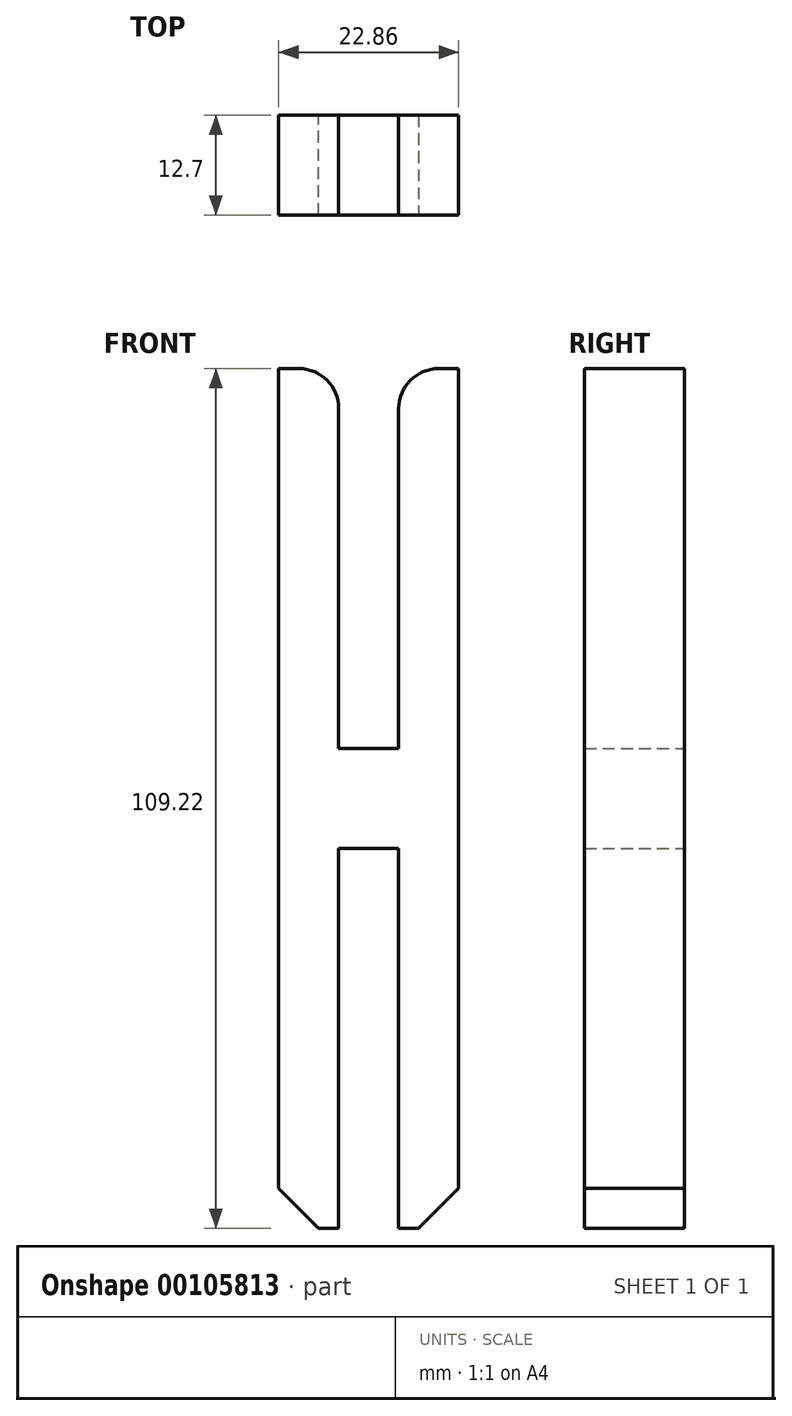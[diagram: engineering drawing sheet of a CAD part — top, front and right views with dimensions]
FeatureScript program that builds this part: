
annotation { "Feature Type Name" : "Feature", "Feature Type Description" : "" }
export const myFeature = defineFeature(function(context is Context, id is Id, definition is map)
    precondition{}
    {
        {
            var Q0;
            Q0=qCreatedBy(makeId("Front.planeOp"),FACE);
            var sketch = newSketch(context, id + "F0", { "sketchPlane" : qUnion([Q0])});
            skLineSegment(sketch, "E0.bottom", {"start": v(11.43, 54.61) * mm, "end": v(-11.43, 54.61) * mm});
            skLineSegment(sketch, "E0.top", {"start": v(11.43, -54.61) * mm, "end": v(-11.43, -54.61) * mm});
            skLineSegment(sketch, "E0.left", {"start": v(11.43, 54.61) * mm, "end": v(11.43, -54.61) * mm});
            skLineSegment(sketch, "E0.right", {"start": v(-11.43, 54.61) * mm, "end": v(-11.43, -54.61) * mm});
            skPoint(sketch, "E0.middle", {"position": v(0, 0) * mm});
            skLineSegment(sketch, "E1.bottom", {"start": v(-3.8, 6.35) * mm, "end": v(3.81, 6.35) * mm});
            skLineSegment(sketch, "E1.top", {"start": v(-3.8, 54.6) * mm, "end": v(3.81, 54.6) * mm});
            skLineSegment(sketch, "E1.left", {"start": v(-3.8, 6.35) * mm, "end": v(-3.8, 54.6) * mm});
            skLineSegment(sketch, "E1.right", {"start": v(3.81, 6.35) * mm, "end": v(3.81, 54.61) * mm});
            skLineSegment(sketch, "E2.bottom", {"start": v(-3.8, -6.35) * mm, "end": v(3.81, -6.35) * mm});
            skLineSegment(sketch, "E2.top", {"start": v(-3.8, -54.61) * mm, "end": v(3.81, -54.61) * mm});
            skLineSegment(sketch, "E2.left", {"start": v(-3.8, -6.35) * mm, "end": v(-3.8, -54.61) * mm});
            skLineSegment(sketch, "E2.right", {"start": v(3.81, -6.35) * mm, "end": v(3.81, -54.61) * mm});
            skSolve(sketch);
        }
        {
            var Q0;
            {var subQ1=sQuery(id+"F0.wireOp",EDGE,"E0.left");Q0=makeQuery(id+"F0.imprint","IMPRINT",FACE,{"disambiguationData":[TD([[makeQuery(id+"F0.imprint","IMPRINT",EDGE,{"derivedFrom":subQ1}),-1.0]])]});}
            extrude(context, id + "F1", {"entities" : qUnion([Q0]), "endBound" : BoundingType.SYMMETRIC, "depth" : 12.7 * mm});
        }
        {
            var Q0;
            Q0=makeQuery(id+"F1.opExtrude","SWEPT_EDGE",EDGE,{"disambiguationData":[OSD([sQuery(id+"F0.wireOp",EDGE,"E0.bottom"),sQuery(id+"F0.wireOp",EDGE,"E1.top"),sQuery(id+"F0.wireOp",EDGE,"E1.left")])]});
            var Q1;
            Q1=makeQuery(id+"F1.opExtrude","SWEPT_EDGE",EDGE,{"disambiguationData":[OSD([sQuery(id+"F0.wireOp",EDGE,"E0.bottom"),sQuery(id+"F0.wireOp",EDGE,"E1.top"),sQuery(id+"F0.wireOp",EDGE,"E1.right")])]});
            fillet(context, id + "F2", {"entities" : qUnion([Q0, Q1]), "radius" : 5.08 * mm, "tangentPropagation" : true, "allowEdgeOverflow" : false});
        }
        {
            var Q0;
            Q0=makeQuery(id+"F1.opExtrude","SWEPT_EDGE",EDGE,{"disambiguationData":[OSD([sQuery(id+"F0.wireOp",EDGE,"E0.top"),sQuery(id+"F0.wireOp",EDGE,"E0.right")])]});
            var Q1;
            Q1=makeQuery(id+"F1.opExtrude","SWEPT_EDGE",EDGE,{"disambiguationData":[OSD([sQuery(id+"F0.wireOp",EDGE,"E0.top"),sQuery(id+"F0.wireOp",EDGE,"E0.left")])]});
            chamfer(context, id + "F3", {"entities" : qUnion([Q0, Q1]), "width" : 5.08 * mm, "tangentPropagation" : true});
        }
    });
